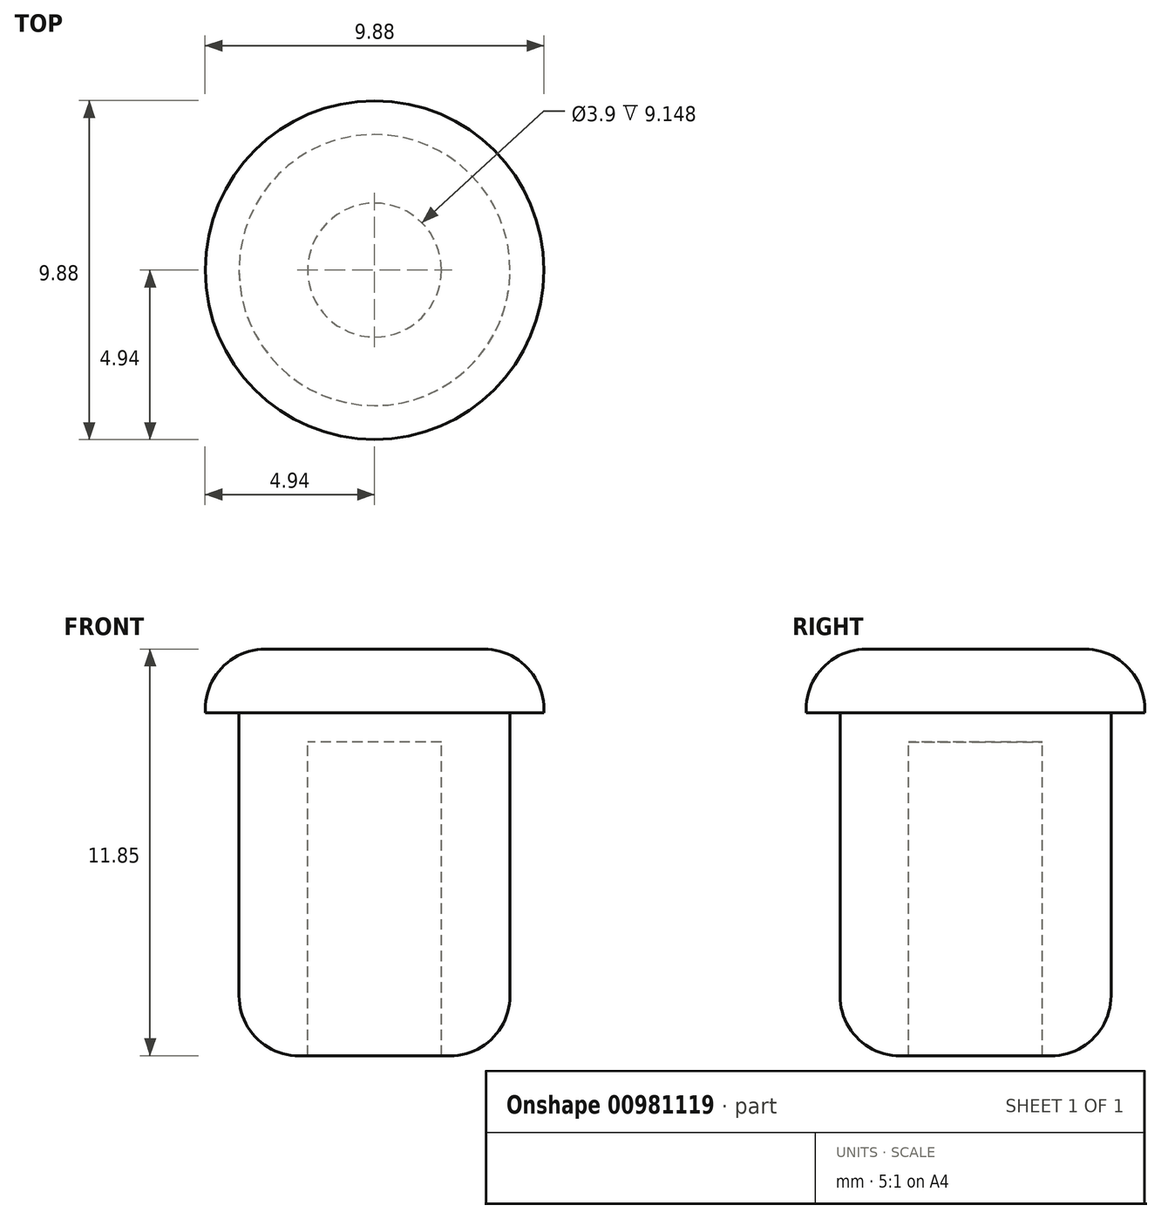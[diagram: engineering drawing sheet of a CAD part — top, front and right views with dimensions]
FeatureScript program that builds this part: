
annotation { "Feature Type Name" : "Feature", "Feature Type Description" : "" }
export const myFeature = defineFeature(function(context is Context, id is Id, definition is map)
    precondition{}
    {
        {
            var Q0;
            Q0=qCreatedBy(makeId("Front.planeOp"),FACE);
            var sketch = newSketch(context, id + "F0", { "sketchPlane" : qUnion([Q0])});
            skLineSegment(sketch, "E0", {"start": v(0, 34.47) * mm, "end": v(0, -31.5) * mm, "construction": true});
            skLineSegment(sketch, "E1", {"start": v(0, 12.16) * mm, "end": v(4.94, 12.16) * mm});
            skLineSegment(sketch, "E2", {"start": v(4.94, 12.16) * mm, "end": v(4.94, 10.3) * mm});
            skLineSegment(sketch, "E3", {"start": v(4.94, 10.3) * mm, "end": v(3.95, 10.3) * mm});
            skLineSegment(sketch, "E4", {"start": v(3.95, 10.3) * mm, "end": v(3.95, 0.3) * mm});
            skLineSegment(sketch, "E5", {"start": v(3.95, 0.3) * mm, "end": v(1.95, 0.3) * mm});
            skLineSegment(sketch, "E6", {"start": v(1.95, 0.3) * mm, "end": v(1.95, 9.45) * mm});
            skLineSegment(sketch, "E7", {"start": v(1.95, 9.45) * mm, "end": v(0, 9.45) * mm});
            skLineSegment(sketch, "E8", {"start": v(0, 9.45) * mm, "end": v(0, 12.16) * mm});
            skSolve(sketch);
        }
        {
            var Q0;
            Q0=makeQuery(id+"F0.imprint","IMPRINT",FACE,{"disambiguationData":[TD([[makeQuery(id+"F0.imprint","IMPRINT",EDGE,{"derivedFrom":sQuery(id+"F0.wireOp",EDGE,"E1")}),-1.0]])]});
            var Q1;
            Q1=sQuery(id+"F0.wireOp",EDGE,"E0");
            revolve(context, id + "F1", {"surfaceOperationType" : NewSurfaceOperationType.NEW, "entities" : qUnion([Q0]), "axis" : qUnion([Q1]), "revolveType" : RevolveType.FULL});
        }
        {
            var Q0;
            Q0=makeQuery(id+"F1.opRevolve","SWEPT_EDGE",EDGE,{"disambiguationData":[OSD([sQuery(id+"F0.wireOp",EDGE,"E1"),sQuery(id+"F0.wireOp",EDGE,"E2")])]});
            var Q1;
            Q1=makeQuery(id+"F1.opRevolve","SWEPT_EDGE",EDGE,{"disambiguationData":[OSD([sQuery(id+"F0.wireOp",EDGE,"E4"),sQuery(id+"F0.wireOp",EDGE,"E5")])]});
            fillet(context, id + "F2", {"entities" : qUnion([Q0, Q1]), "radius" : 1.75 * mm, "tangentPropagation" : true, "allowEdgeOverflow" : false});
        }
    });
